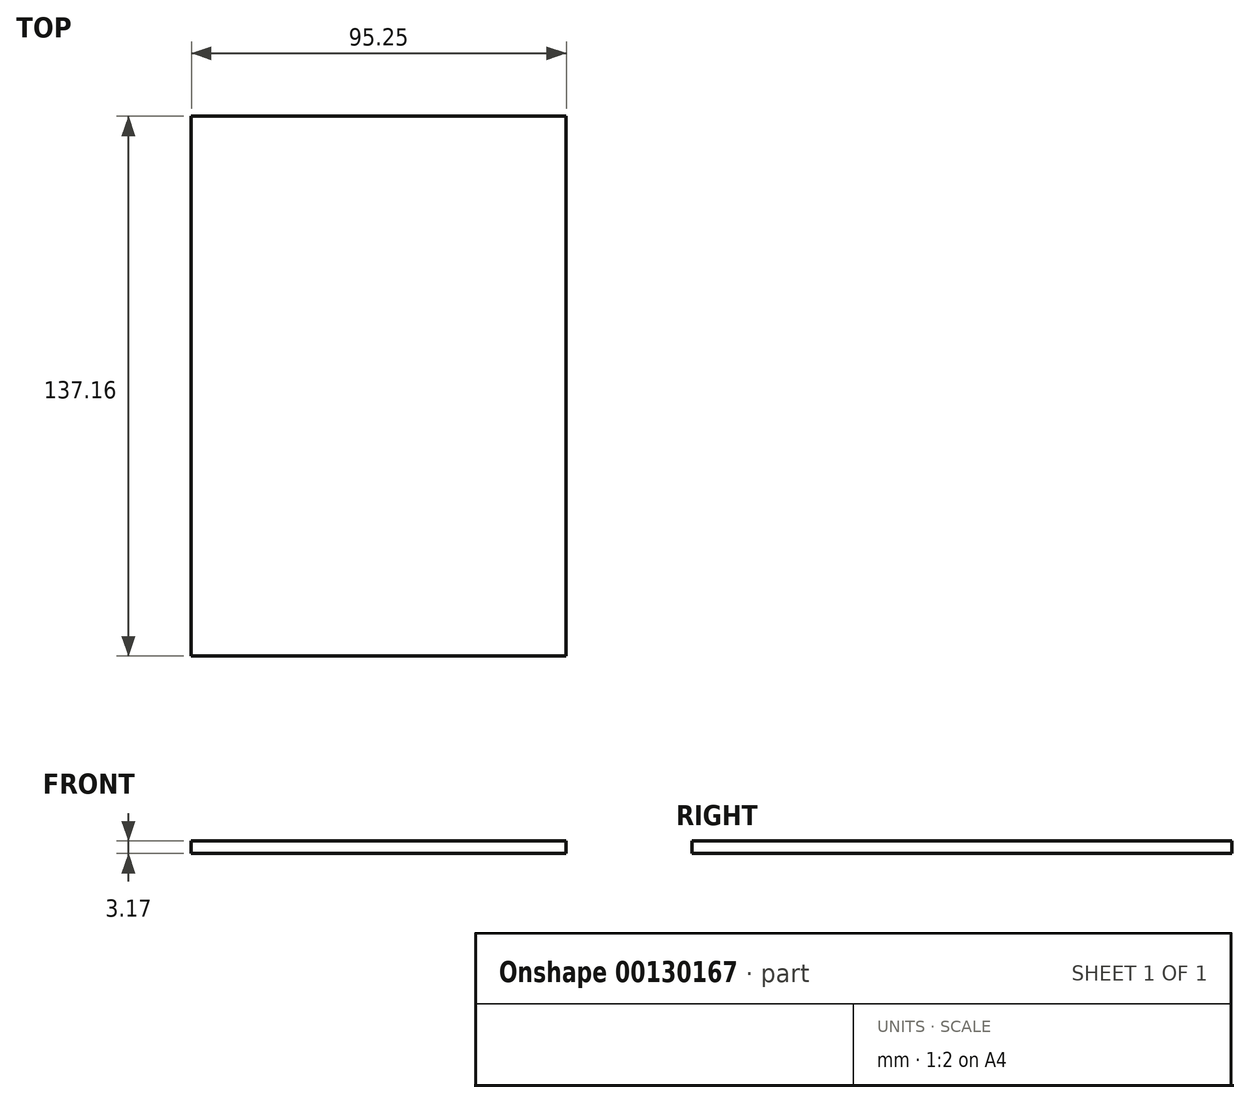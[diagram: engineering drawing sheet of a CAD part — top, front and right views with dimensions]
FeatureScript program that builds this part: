
annotation { "Feature Type Name" : "Feature", "Feature Type Description" : "" }
export const myFeature = defineFeature(function(context is Context, id is Id, definition is map)
    precondition{}
    {
        {
            var Q0;
            Q0=qCreatedBy(makeId("Top.planeOp"),FACE);
            var sketch = newSketch(context, id + "F0", { "sketchPlane" : qUnion([Q0])});
            skLineSegment(sketch, "E0.bottom", {"start": v(-42.47, 85.09) * mm, "end": v(52.78, 85.09) * mm});
            skLineSegment(sketch, "E0.top", {"start": v(-42.47, -52.07) * mm, "end": v(52.78, -52.07) * mm});
            skLineSegment(sketch, "E0.left", {"start": v(-42.47, 85.09) * mm, "end": v(-42.47, -52.07) * mm});
            skLineSegment(sketch, "E0.right", {"start": v(52.78, 85.09) * mm, "end": v(52.78, -52.07) * mm});
            skSolve(sketch);
        }
        {
            var Q0;
            Q0=makeQuery(id+"F0.imprint","IMPRINT",FACE,{"disambiguationData":[TD([[makeQuery(id+"F0.imprint","IMPRINT",EDGE,{"derivedFrom":sQuery(id+"F0.wireOp",EDGE,"E0.bottom")}),-1.0]])]});
            extrude(context, id + "F1", {"entities" : qUnion([Q0]), "depth" : 3.17 * mm});
        }
    });
